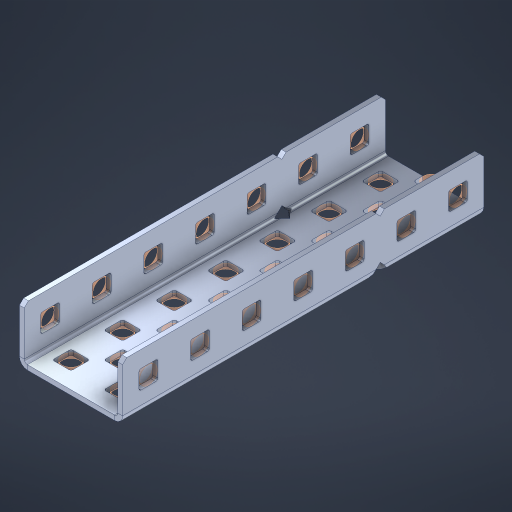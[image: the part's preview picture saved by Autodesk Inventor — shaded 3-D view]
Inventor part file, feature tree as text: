
AUTODESK INVENTOR PART (.ipt)
format: ipt  version: 2023 (Build 270158000, 158)  size: 772,608 bytes
history: native  units: in
note: dims shown in document units (in); Inventor stores cm internally (conversion verified against a paired STEP export)
features: other x42, extrude x33, sheet_metal_op x11, sketch x10, pattern_linear x2, mirror x1, chamfer x1
ambient origin geometry x8: Origin, YZ Plane, XZ Plane, XY Plane, X Axis, Y Axis, Z Axis, Center Point
bodies: Solid1 (feature_tree), Body (feature_tree)
feature tree (100):
  sheet_metal_op  "Flanges"
  other  "Flange Pattern Plane"
  other  "Flange Pattern Sketch"
  sheet_metal_op  "Flange Pattern"
  sheet_metal_op  "Body Pattern"
  pattern_linear  "Center Pattern"  Spacing1=0.0469in  [1 undecoded]
  other  "Arc Length"
  mirror  "Notch Mirror"
  pattern_linear  "Notch Pattern"  Spacing1=0.182in  [1 undecoded]
  chamfer  "End Chamfer"
  extrude  "Half Cut"  Depth=0.02in
  sketch  "Sketch1"  dims[d0=1.0in]
  other  "Plate1"
  sketch  "Sketch2"  dims[d1=3.5in]
  other  "Plate2"
  sheet_metal_op  "Bend1"
  sheet_metal_op  "Corner1"
  sketch  "Sketch3"  dims[d2=0.0469in]
  sketch  "Sketch7"  dims[d3=0.0469in]
  other  "Srf1"
  other  "Srf2"
  sketch  "Sketch8"  dims[d4=0.0234in]
  sketch  "Sketch9"  dims[d5=0.0938in]
  other  "Srf91"
  sheet_metal_op  "Body Pattern Sketch"
  other  "Srf92"
  sketch  "Sketch13"  dims[d6=0.0469in]
  sketch  "Sketch14"  dims[d7=0.5in d8=90.0deg d9=0.0312in]
  sketch  "Sketch15"  dims[d10=0.1875in]
  sketch  "Sketch16"  dims[d11=0.0469in d12=0.0469in d16=0.182in d17=0.02in d18=0.0469in d19=0.0in d20=0.25in d21=0.25in d38=2.7559in d40=0.5in d41=0.7874in d43=1.0in d46=0.172in d47=1.0in d48=0.0in d49=0.182in d50=0.02in d51=0.25in d52=0.25in d53=0.0469in d54=0.0in d55=0.172in d56=1.0in d57=0.0in d58=0.25in d60=2.7559in d62=0.5in d63=0.7874in d65=0.5in d85=0.1227in d86=0.1659in d88=0.04in d89=0.0469in d90=0.0in d91=0.04in d92=0.0491in d95=2.5in d96=0.04in d97=0.25in d98=45.0deg d99=0.25in d100=0.5in d101=0.0in d102=2.497in d106=0.182in d107=0.02in d108=0.5in d109=0.5in d110=0.0469in d111=0.0in d112=0.172in d113=0.5in d114=0.0in d117=0.5in d118=0.5in d119=0.5in]
  other  "Srf786"
  other  "Srf823"
  other  "Srf824"
  other  "Srf825"
  other  "Srf826"
  other  "Srf827"
  other  "Srf828"
  other  "Srf829"
  other  "Srf856"
  other  "Srf857"
  other  "Srf858"
  other  "Srf859"
  other  "Srf860"
  other  "Srf861"
  other  "Srf862"
  other  "Srf889"
  other  "Srf890"
  other  "Srf891"
  other  "Srf892"
  other  "Srf893"
  other  "Srf894"
  other  "Srf922"
  other  "Srf923"
  other  "Srf924"
  other  "Srf925"
  other  "Srf926"
  other  "Srf959"
  other  "Srf960"
  other  "Srf961"
  other  "Srf962"
  other  "Srf963"
  sheet_metal_op  "Flange Stamp"
  sheet_metal_op  "Flange Circle"
  sheet_metal_op  "Body Stamp"
  sheet_metal_op  "Body Circle"
  other  "Center Stamp"
  other  "Center Circle"
  sheet_metal_op  "Notch"
  extrude  "ExtrusionSrf2"  Depth=0.0469in
  extrude  "ExtrusionSrf92"  TaperAngle=0.0deg  [1 undecoded]
  extrude  "ExtrusionSrf823"  Depth=0.5in
  extrude  "ExtrusionSrf824"  Depth=0.5in
  extrude  "ExtrusionSrf825"  Depth=0.5in
  extrude  "ExtrusionSrf826"  Depth=0.5in
  extrude  "ExtrusionSrf827"  Depth=1.0in TaperAngle=0.0deg
  extrude  "ExtrusionSrf828"  Depth=0.5in
  extrude  "ExtrusionSrf829"  Depth=0.02in
  extrude  "ExtrusionSrf856"  Depth=0.5in
  extrude  "ExtrusionSrf857"  Depth=0.5in
  extrude  "ExtrusionSrf858"  Depth=0.0469in
  extrude  "ExtrusionSrf859"  TaperAngle=0.0deg  [1 undecoded]
  extrude  "ExtrusionSrf860"  Depth=0.5in
  extrude  "ExtrusionSrf861"  Depth=1.0in TaperAngle=0.0deg
  extrude  "ExtrusionSrf862"  Depth=0.5in
  extrude  "ExtrusionSrf889"  Depth=0.5in
  extrude  "ExtrusionSrf890"  Depth=0.5in
  extrude  "ExtrusionSrf891"  Depth=0.5in
  extrude  "ExtrusionSrf892"  Depth=0.5in
  extrude  "ExtrusionSrf893"  Depth=0.5in
  extrude  "ExtrusionSrf894"  Depth=0.0469in
  extrude  "ExtrusionSrf922"  TaperAngle=0.0deg  [1 undecoded]
  extrude  "ExtrusionSrf923"  Depth=0.5in
  extrude  "ExtrusionSrf924"  Depth=0.5in
  extrude  "ExtrusionSrf925"  Depth=2.5in
  extrude  "ExtrusionSrf926"  Depth=0.5in TaperAngle=45.0deg
  extrude  "ExtrusionSrf959"  Depth=0.5in
  extrude  "ExtrusionSrf960"  Depth=0.5in TaperAngle=0.0deg
  extrude  "ExtrusionSrf961"  Depth=0.5in
  extrude  "ExtrusionSrf962"  Depth=0.5in
  extrude  "ExtrusionSrf963"  Depth=0.02in
note: 5 required parameter values undecoded (feature->parameter linkage not recoverable at this tier; creation-order binding heuristic only, values carry confidence <= 0.55)
